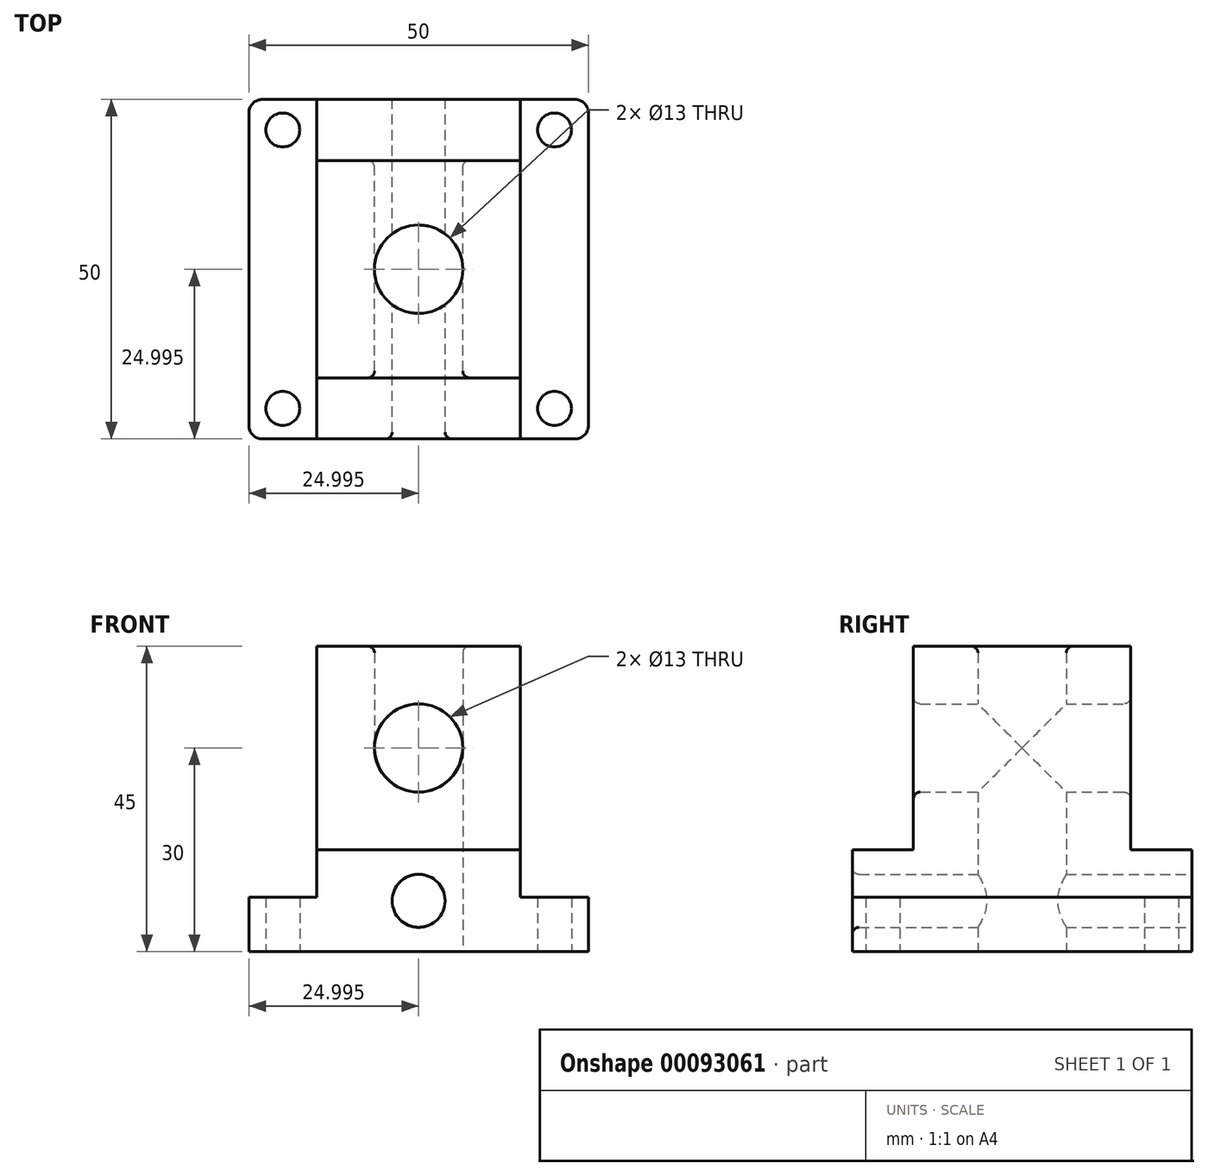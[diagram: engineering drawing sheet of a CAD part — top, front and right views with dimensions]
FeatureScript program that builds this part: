
annotation { "Feature Type Name" : "Feature", "Feature Type Description" : "" }
export const myFeature = defineFeature(function(context is Context, id is Id, definition is map)
    precondition{}
    {
        {
            var Q0;
            Q0=qCreatedBy(makeId("Top.planeOp"),FACE);
            var sketch = newSketch(context, id + "F0", { "sketchPlane" : qUnion([Q0])});
            skLineSegment(sketch, "E0.bottom", {"start": v(-27.04, 15.64) * mm, "end": v(-17.04, 15.64) * mm});
            skLineSegment(sketch, "E0.top", {"start": v(-27.04, -34.36) * mm, "end": v(-17.04, -34.36) * mm});
            skLineSegment(sketch, "E0.left", {"start": v(-27.04, 15.64) * mm, "end": v(-27.04, -34.36) * mm});
            skLineSegment(sketch, "E0.right", {"start": v(22.96, 15.64) * mm, "end": v(22.96, -34.36) * mm});
            skLineSegment(sketch, "E1", {"start": v(-17.04, -34.36) * mm, "end": v(12.96, -34.36) * mm});
            skLineSegment(sketch, "E2", {"start": v(12.96, -34.36) * mm, "end": v(22.96, -34.36) * mm});
            skLineSegment(sketch, "E3", {"start": v(-17.04, -34.36) * mm, "end": v(-17.04, -25.36) * mm});
            skLineSegment(sketch, "E4", {"start": v(12.96, -34.36) * mm, "end": v(12.96, -25.36) * mm});
            skLineSegment(sketch, "E5", {"start": v(-17.04, 6.64) * mm, "end": v(-17.04, 15.64) * mm});
            skLineSegment(sketch, "E6", {"start": v(-17.04, -25.36) * mm, "end": v(-17.04, 6.64) * mm});
            skLineSegment(sketch, "E7", {"start": v(-17.04, 6.64) * mm, "end": v(12.96, 6.64) * mm});
            skLineSegment(sketch, "E8", {"start": v(-17.04, -25.36) * mm, "end": v(12.96, -25.36) * mm});
            skPoint(sketch, "E9", {"position": v(-2.04, -9.36) * mm});
            skPoint(sketch, "E9.positionSnap0", {"position": v(-2.04, 6.64) * mm});
            skPoint(sketch, "E9.positionSnap1", {"position": v(-17.04, -9.36) * mm});
            skCircle(sketch, "E10", {"center": v(-2.04, -9.36) * mm, "radius": 6.5 * mm});
            skLineSegment(sketch, "E11", {"start": v(-17.04, 15.64) * mm, "end": v(12.96, 15.64) * mm});
            skLineSegment(sketch, "E12", {"start": v(12.96, 15.64) * mm, "end": v(22.96, 15.64) * mm});
            skLineSegment(sketch, "E13", {"start": v(12.96, 6.64) * mm, "end": v(12.96, 15.64) * mm});
            skLineSegment(sketch, "E14", {"start": v(12.96, -25.36) * mm, "end": v(12.96, 6.64) * mm});
            skCircle(sketch, "E15", {"center": v(-22.04, 11.14) * mm, "radius": 2.5 * mm});
            skPoint(sketch, "E15.centerSnap0", {"position": v(-22.04, 15.64) * mm});
            skPoint(sketch, "E15.centerSnap1", {"position": v(-17.04, 11.14) * mm});
            skCircle(sketch, "E16", {"center": v(17.96, 11.14) * mm, "radius": 2.5 * mm});
            skPoint(sketch, "E16.centerSnap0", {"position": v(17.96, 15.64) * mm});
            skCircle(sketch, "E17", {"center": v(17.96, -29.86) * mm, "radius": 2.5 * mm});
            skPoint(sketch, "E17.centerSnap0", {"position": v(17.96, -34.36) * mm});
            skPoint(sketch, "E17.centerSnap1", {"position": v(12.96, -29.86) * mm});
            skCircle(sketch, "E18", {"center": v(-22.04, -29.86) * mm, "radius": 2.5 * mm});
            skPoint(sketch, "E18.centerSnap0", {"position": v(-17.04, -29.86) * mm});
            skPoint(sketch, "E18.centerSnap1", {"position": v(-22.04, -34.36) * mm});
            skSolve(sketch);
        }
        {
            var Q0;
            Q0 = qSketchRegion(id + "F0", true);
            var Q1;
            Q1=makeQuery(id+"F0.imprint","IMPRINT",FACE,{"disambiguationData":[TD([[makeQuery(id+"F0.imprint","IMPRINT",EDGE,{"derivedFrom":sQuery(id+"F0.wireOp",EDGE,"E6")}),-1.0]])]});
            extrude(context, id + "F1", {"entities" : qUnion([Q0, Q1]), "depth" : 8 * mm});
        }
        {
            var Q0;
            Q0=makeQuery(id+"F0.imprint","IMPRINT",FACE,{"disambiguationData":[TD([[makeQuery(id+"F0.imprint","IMPRINT",EDGE,{"derivedFrom":sQuery(id+"F0.wireOp",EDGE,"E5")}),-1.0]])]});
            var Q1;
            Q1=makeQuery(id+"F0.imprint","IMPRINT",FACE,{"disambiguationData":[TD([[makeQuery(id+"F0.imprint","IMPRINT",EDGE,{"derivedFrom":sQuery(id+"F0.wireOp",EDGE,"E1")}),1.0]])]});
            var Q2;
            Q2=makeQuery(id+"F0.imprint","IMPRINT",FACE,{"disambiguationData":[TD([[makeQuery(id+"F0.imprint","IMPRINT",EDGE,{"derivedFrom":sQuery(id+"F0.wireOp",EDGE,"E6")}),-1.0]])]});
            extrude(context, id + "F2", {"entities" : qUnion([Q0, Q1, Q2]), "operationType" : NewBodyOperationType.ADD, "depth" : 15 * mm});
        }
        {
            var Q0;
            Q0=makeQuery(id+"F0.imprint","IMPRINT",FACE,{"disambiguationData":[TD([[makeQuery(id+"F0.imprint","IMPRINT",EDGE,{"derivedFrom":sQuery(id+"F0.wireOp",EDGE,"E6")}),-1.0]])]});
            extrude(context, id + "F3", {"entities" : qUnion([Q0]), "operationType" : NewBodyOperationType.ADD, "depth" : 45 * mm});
        }
        {
            var Q0;
            {var subQ0=sQuery(id+"F0.wireOp",EDGE,"E11");Q0=makeQuery(id+"F2.boolean.opBoolean","MERGE",FACE,{"derivedFrom":[makeQuery(id+"F1.opExtrude","SWEPT_FACE",FACE,{"disambiguationData":[OSD([sQuery(id+"F0.wireOp",EDGE,"E0.bottom"),subQ0,sQuery(id+"F0.wireOp",EDGE,"E12")])]}),makeQuery(id+"F2.opExtrude","SWEPT_FACE",FACE,{"disambiguationData":[OSD([subQ0])]})]});}
            var sketch = newSketch(context, id + "F4", { "sketchPlane" : qUnion([Q0])});
            skLineSegment(sketch, "E19.0.0", {"start": v(-22.96, 8) * mm, "end": v(-22.96, 0) * mm});
            skLineSegment(sketch, "E19.0.1", {"start": v(-22.96, 0) * mm, "end": v(27.04, 0) * mm});
            skLineSegment(sketch, "E19.0.2", {"start": v(27.04, 0) * mm, "end": v(27.04, 8) * mm});
            skLineSegment(sketch, "E19.0.3", {"start": v(27.04, 8) * mm, "end": v(17.04, 8) * mm});
            skLineSegment(sketch, "E19.0.4", {"start": v(17.04, 0) * mm, "end": v(17.04, 15) * mm});
            skLineSegment(sketch, "E19.0.5", {"start": v(17.04, 15) * mm, "end": v(-12.96, 15) * mm});
            skLineSegment(sketch, "E19.0.6", {"start": v(-12.96, 15) * mm, "end": v(-12.96, 0) * mm});
            skLineSegment(sketch, "E19.0.7", {"start": v(-12.96, 8) * mm, "end": v(-22.96, 8) * mm});
            skPoint(sketch, "E20", {"position": v(2.04, 7.5) * mm});
            skPoint(sketch, "E20.positionSnap0", {"position": v(2.04, 15) * mm});
            skPoint(sketch, "E20.positionSnap1", {"position": v(-12.96, 7.5) * mm});
            skCircle(sketch, "E21", {"center": v(2.04, 7.5) * mm, "radius": 3.9 * mm});
            skLineSegment(sketch, "E22.0.0", {"start": v(-12.96, 45) * mm, "end": v(-12.96, 15) * mm});
            skLineSegment(sketch, "E22.0.1", {"start": v(-12.96, 15) * mm, "end": v(17.04, 15) * mm});
            skLineSegment(sketch, "E22.0.2", {"start": v(17.04, 15) * mm, "end": v(17.04, 45) * mm});
            skLineSegment(sketch, "E22.0.3", {"start": v(17.04, 45) * mm, "end": v(-12.96, 45) * mm});
            skPoint(sketch, "E23", {"position": v(2.04, 30) * mm});
            skPoint(sketch, "E23.positionSnap0", {"position": v(2.04, 45) * mm});
            skPoint(sketch, "E23.positionSnap1", {"position": v(-12.96, 30) * mm});
            skCircle(sketch, "E24", {"center": v(2.04, 30) * mm, "radius": 6.5 * mm});
            skSolve(sketch);
        }
        {
            var Q0;
            Q0=makeQuery(id+"F4.imprint","IMPRINT",FACE,{"disambiguationData":[TD([[makeQuery(id+"F4.imprint","IMPRINT",EDGE,{"derivedFrom":sQuery(id+"F4.wireOp",EDGE,"E24")}),1.0]])]});
            var Q1;
            Q1=makeQuery(id+"F4.imprint","IMPRINT",FACE,{"disambiguationData":[TD([[makeQuery(id+"F4.imprint","IMPRINT",EDGE,{"derivedFrom":sQuery(id+"F4.wireOp",EDGE,"E21")}),1.0]])]});
            extrude(context, id + "F5", {"entities" : qUnion([Q0, Q1]), "operationType" : NewBodyOperationType.REMOVE, "endBound" : BoundingType.THROUGH_ALL, "oppositeDirection" : true, "depth" : 25 * mm});
        }
        {
            var Q0;
            Q0=makeQuery(id+"F5.boolean.opBoolean","COPY",EDGE,{"derivedFrom":makeQuery(id+"F5.opExtrude","CAP_EDGE",EDGE,{"disambiguationData":[OSD([sQuery(id+"F4.wireOp",EDGE,"E21")])],"isStart":true})});
            var Q1;
            {var subQ0=sQuery(id+"F0.wireOp",EDGE,"E1");Q1=makeQuery(id+"F5.boolean.opBoolean","INTERSECT",EDGE,{"derivedFrom":[makeQuery(id+"F2.boolean.opBoolean","MERGE",FACE,{"derivedFrom":[makeQuery(id+"F1.opExtrude","SWEPT_FACE",FACE,{"disambiguationData":[OSD([sQuery(id+"F0.wireOp",EDGE,"E0.top"),subQ0,sQuery(id+"F0.wireOp",EDGE,"E2")])]}),makeQuery(id+"F2.opExtrude","SWEPT_FACE",FACE,{"disambiguationData":[OSD([subQ0])]})]}),makeQuery(id+"F5.opExtrude","SWEPT_FACE",FACE,{"disambiguationData":[OSD([sQuery(id+"F4.wireOp",EDGE,"E21")])]})]});}
            var Q2;
            Q2=makeQuery(id+"F3.opExtrude","CAP_EDGE",EDGE,{"disambiguationData":[OSD([sQuery(id+"F0.wireOp",EDGE,"E10")])],"isStart":false});
            var Q3;
            Q3=makeQuery(id+"F5.boolean.opBoolean","INTERSECT",EDGE,{"derivedFrom":[makeQuery(id+"F3.opExtrude","SWEPT_FACE",FACE,{"disambiguationData":[OSD([sQuery(id+"F0.wireOp",EDGE,"E8")])]}),makeQuery(id+"F5.opExtrude","SWEPT_FACE",FACE,{"disambiguationData":[OSD([sQuery(id+"F4.wireOp",EDGE,"E24")])]})]});
            var Q4;
            Q4=makeQuery(id+"F5.boolean.opBoolean","INTERSECT",EDGE,{"derivedFrom":[makeQuery(id+"F3.opExtrude","SWEPT_FACE",FACE,{"disambiguationData":[OSD([sQuery(id+"F0.wireOp",EDGE,"E7")])]}),makeQuery(id+"F5.opExtrude","SWEPT_FACE",FACE,{"disambiguationData":[OSD([sQuery(id+"F4.wireOp",EDGE,"E24")])]})]});
            fillet(context, id + "F6", {"entities" : qUnion([Q0, Q1, Q2, Q3, Q4]), "radius" : 1 * mm, "tangentPropagation" : true, "allowEdgeOverflow" : false});
        }
        {
            var Q0;
            Q0=makeQuery(id+"F1.opExtrude","SWEPT_EDGE",EDGE,{"disambiguationData":[OSD([sQuery(id+"F0.wireOp",EDGE,"E0.top"),sQuery(id+"F0.wireOp",EDGE,"E0.left")])]});
            var Q1;
            Q1=makeQuery(id+"F1.opExtrude","SWEPT_EDGE",EDGE,{"disambiguationData":[OSD([sQuery(id+"F0.wireOp",EDGE,"E0.right"),sQuery(id+"F0.wireOp",EDGE,"E2")])]});
            var Q2;
            Q2=makeQuery(id+"F1.opExtrude","SWEPT_EDGE",EDGE,{"disambiguationData":[OSD([sQuery(id+"F0.wireOp",EDGE,"E0.right"),sQuery(id+"F0.wireOp",EDGE,"E12")])]});
            var Q3;
            Q3=makeQuery(id+"F1.opExtrude","SWEPT_EDGE",EDGE,{"disambiguationData":[OSD([sQuery(id+"F0.wireOp",EDGE,"E0.bottom"),sQuery(id+"F0.wireOp",EDGE,"E0.left")])]});
            fillet(context, id + "F7", {"entities" : qUnion([Q0, Q1, Q2, Q3]), "radius" : 2 * mm, "tangentPropagation" : true, "allowEdgeOverflow" : false});
        }
    });
